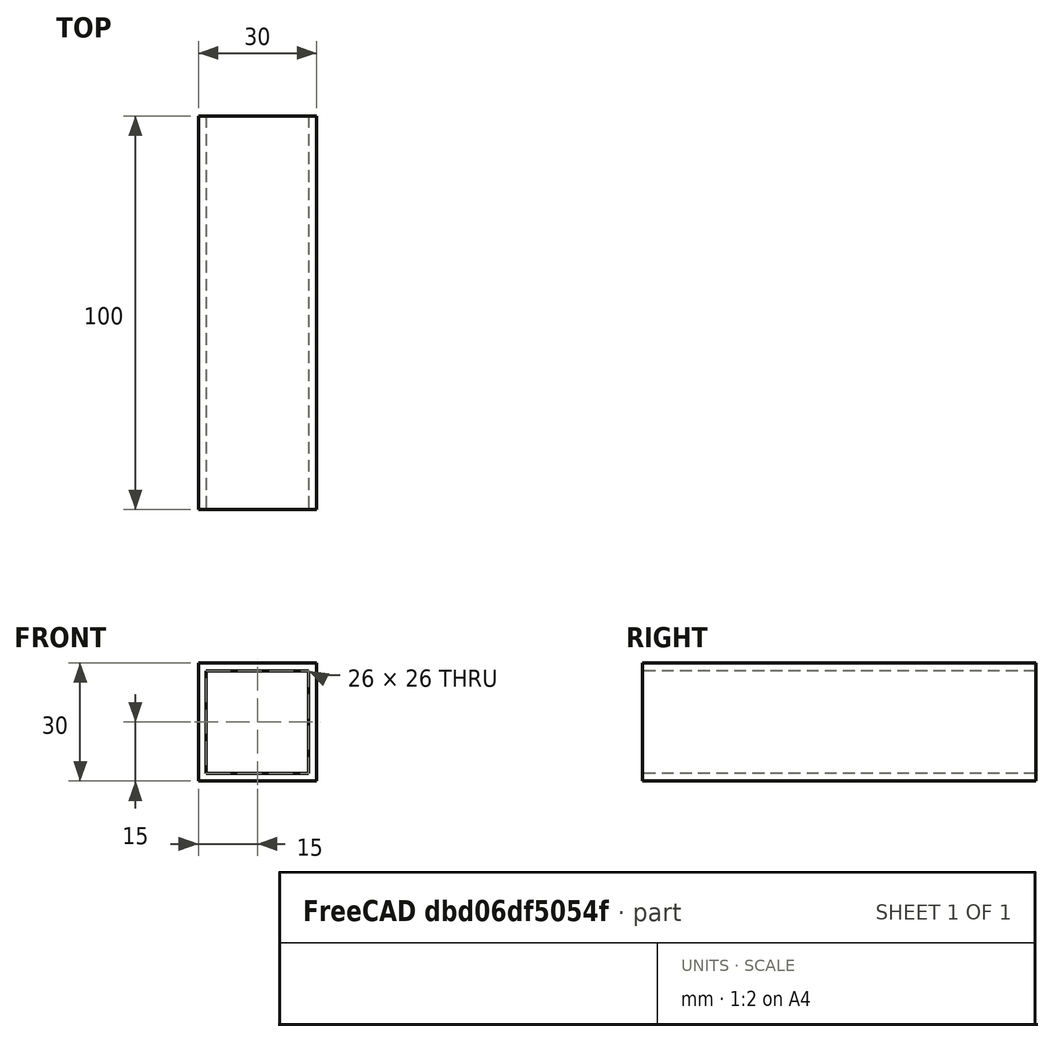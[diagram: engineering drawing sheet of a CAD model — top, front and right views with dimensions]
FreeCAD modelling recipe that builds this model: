
FCSTD DOCUMENT  (FreeCAD 0.20R29603 (Git))
Label: AluProfil 30x30x2_quer_kurz
License: All rights reserved
LicenseURL: http://en.wikipedia.org/wiki/All_rights_reserved
objects: Sketcher::SketchObject×1, PartDesign::Pad×1, PartDesign::Body×1
note: 4 computed .brp shape members not serialized (recipe doc carries the construction recipe); baked Part::Feature solids carry a one-line shape summary decoded from their .brp

FEATURE [Sketcher::SketchObject] Sketch001
  FullyConstrained = true
  MapMode = 5
  Placement = pos=(0,0,0) rot=(1,0,0;1.5708rad)
  Support = -> [XZ_Plane001]
  sketch-geometry (8):
    g0: LineSegment StartX=0 StartY=0 StartZ=0 EndX=30 EndY=0 EndZ=0
    g1: LineSegment StartX=30 StartY=0 StartZ=0 EndX=30 EndY=-30 EndZ=0
    g2: LineSegment StartX=30 StartY=-30 StartZ=0 EndX=0 EndY=-30 EndZ=0
    g3: LineSegment StartX=0 StartY=-30 StartZ=0 EndX=0 EndY=0 EndZ=0
    g4: LineSegment StartX=2 StartY=-2 StartZ=0 EndX=28 EndY=-2 EndZ=0
    g5: LineSegment StartX=28 StartY=-2 StartZ=0 EndX=28 EndY=-28 EndZ=0
    g6: LineSegment StartX=28 StartY=-28 StartZ=0 EndX=2 EndY=-28 EndZ=0
    g7: LineSegment StartX=2 StartY=-28 StartZ=0 EndX=2 EndY=-2 EndZ=0
  constraints (24):
    c: Coincident(g0,g1)
    c: Coincident(g1,g2)
    c: Coincident(g2,g3)
    c: Coincident(g3,g0)
    c: Horizontal(g0)
    c: Horizontal(g2)
    c: Vertical(g1)
    c: Vertical(g3)
    c: PointOnObject(g0,g-2)
    c: Coincident(g4,g5)
    c: Coincident(g5,g6)
    c: Coincident(g6,g7)
    c: Coincident(g7,g4)
    c: Horizontal(g4)
    c: Horizontal(g6)
    c: Vertical(g5)
    c: Vertical(g7)
    c: Distance(g0) = 30
    c: Distance(g1) = 30
    c: Distance(g4) = 26
    c: Distance(g5) = 26
    c: Distance(g2,g7) = 2
    c: Distance(g4,g0) = 2
    c: PointOnObject(g0,g-1)
FEATURE [PartDesign::Pad] Pad001  label="länge 840mm"
  Direction = (0,-1,-2e-16)
  Length = 100
  Length2 = 10
  Placement = pos=(0,0,0) rot=(1,0,0;1.5708rad)
  Profile = -> Sketch001
  ReferenceAxis = -> Sketch001 [N_Axis]
  Type = 0
FEATURE [PartDesign::Body] Body001  label="AluProfil 30x30x2 002"
  Group = -> [Sketch001,Pad001]
  Origin = -> Origin001
  Placement = pos=(-240,390,0) rot=(0,0,1;0rad)
  Tip = -> Pad001
